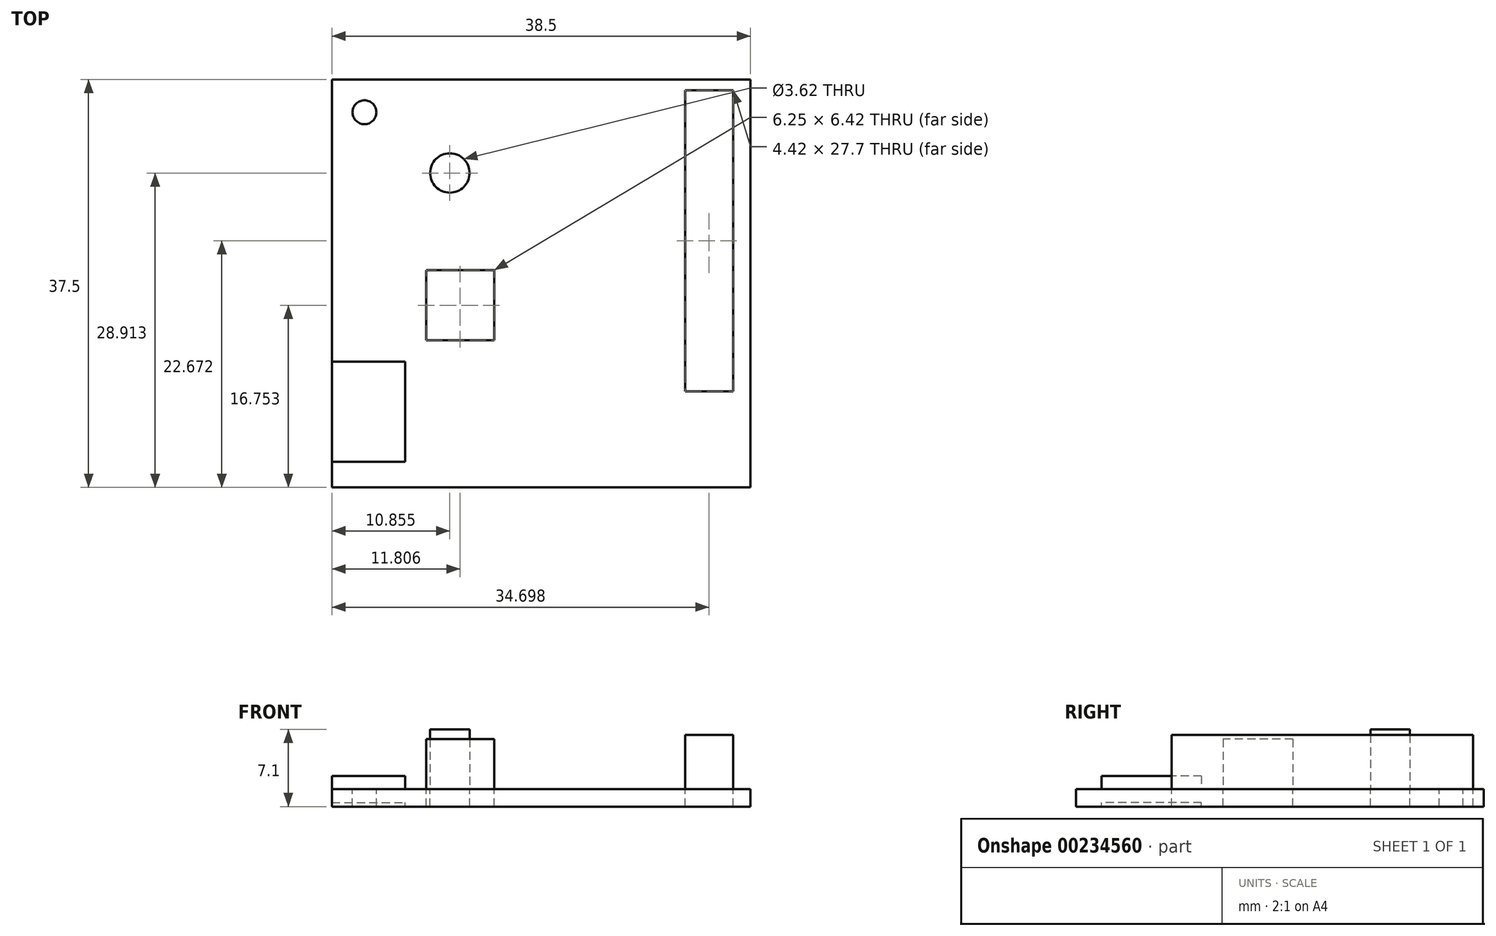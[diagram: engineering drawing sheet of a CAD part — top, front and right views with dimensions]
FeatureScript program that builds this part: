
annotation { "Feature Type Name" : "Feature", "Feature Type Description" : "" }
export const myFeature = defineFeature(function(context is Context, id is Id, definition is map)
    precondition{}
    {
        {
            var Q0;
            Q0=qCreatedBy(makeId("Top.planeOp"),FACE);
            var sketch = newSketch(context, id + "F0", { "sketchPlane" : qUnion([Q0])});
            skLineSegment(sketch, "E0.bottom", {"start": v(19.25, 18.75) * mm, "end": v(-19.25, 18.75) * mm});
            skLineSegment(sketch, "E0.top", {"start": v(19.25, -18.75) * mm, "end": v(-19.25, -18.75) * mm});
            skLineSegment(sketch, "E0.left", {"start": v(19.25, 18.75) * mm, "end": v(19.25, -18.75) * mm});
            skLineSegment(sketch, "E0.right", {"start": v(-19.25, 18.75) * mm, "end": v(-19.25, -18.75) * mm});
            skPoint(sketch, "E0.middle", {"position": v(0, 0) * mm});
            skLineSegment(sketch, "E1.bottom", {"start": v(17.66, 17.77) * mm, "end": v(13.24, 17.77) * mm});
            skLineSegment(sketch, "E1.top", {"start": v(17.66, -9.93) * mm, "end": v(13.24, -9.93) * mm});
            skLineSegment(sketch, "E1.left", {"start": v(17.66, 17.77) * mm, "end": v(17.66, -9.93) * mm});
            skLineSegment(sketch, "E1.right", {"start": v(13.24, 17.77) * mm, "end": v(13.24, -9.93) * mm});
            skLineSegment(sketch, "E2.bottom", {"start": v(-4.32, 1.21) * mm, "end": v(-10.57, 1.21) * mm});
            skLineSegment(sketch, "E2.top", {"start": v(-4.32, -5.2) * mm, "end": v(-10.57, -5.2) * mm});
            skLineSegment(sketch, "E2.left", {"start": v(-4.32, 1.21) * mm, "end": v(-4.32, -5.2) * mm});
            skLineSegment(sketch, "E2.right", {"start": v(-10.57, 1.21) * mm, "end": v(-10.57, -5.2) * mm});
            skPoint(sketch, "E2.middle", {"position": v(-7.44, -2) * mm});
            skCircle(sketch, "E3", {"center": v(-8.4, 10.16) * mm, "radius": 1.81 * mm});
            skPoint(sketch, "E4", {"position": v(-16.25, 15.75) * mm});
            skLineSegment(sketch, "E5.bottom", {"start": v(-19.25, -7.2) * mm, "end": v(-12.5, -7.2) * mm});
            skLineSegment(sketch, "E5.top", {"start": v(-19.25, -16.4) * mm, "end": v(-12.5, -16.4) * mm});
            skLineSegment(sketch, "E5.left", {"start": v(-19.25, -7.2) * mm, "end": v(-19.25, -16.4) * mm});
            skLineSegment(sketch, "E5.right", {"start": v(-12.5, -7.2) * mm, "end": v(-12.5, -16.4) * mm});
            skSolve(sketch);
        }
        {
            var Q0;
            Q0=makeQuery(id+"F0.imprint","IMPRINT",FACE,{"disambiguationData":[TD([[makeQuery(id+"F0.imprint","IMPRINT",EDGE,{"derivedFrom":sQuery(id+"F0.wireOp",EDGE,"E0.bottom")}),1.0]])]});
            extrude(context, id + "F1", {"entities" : qUnion([Q0]), "oppositeDirection" : true, "depth" : 1.6 * mm});
        }
        {
            var Q0;
            Q0=makeQuery(id+"F0.imprint","IMPRINT",FACE,{"disambiguationData":[TD([[makeQuery(id+"F0.imprint","IMPRINT",EDGE,{"derivedFrom":sQuery(id+"F0.wireOp",EDGE,"E1.bottom")}),1.0]])]});
            extrude(context, id + "F2", {"entities" : qUnion([Q0]), "operationType" : NewBodyOperationType.ADD, "depth" : 5 * mm});
        }
        {
            var Q0;
            Q0=makeQuery(id+"F0.imprint","IMPRINT",FACE,{"disambiguationData":[TD([[makeQuery(id+"F0.imprint","IMPRINT",EDGE,{"derivedFrom":sQuery(id+"F0.wireOp",EDGE,"E2.bottom")}),1.0]])]});
            extrude(context, id + "F3", {"entities" : qUnion([Q0]), "operationType" : NewBodyOperationType.ADD, "depth" : 4.6 * mm});
        }
        {
            var Q0;
            Q0=makeQuery(id+"F0.imprint","IMPRINT",FACE,{"disambiguationData":[TD([[makeQuery(id+"F0.imprint","IMPRINT",EDGE,{"derivedFrom":sQuery(id+"F0.wireOp",EDGE,"E3")}),1.0]])]});
            extrude(context, id + "F4", {"entities" : qUnion([Q0]), "operationType" : NewBodyOperationType.ADD, "depth" : 5.5 * mm});
        }
        {
            var Q0;
            Q0=sQuery(id+"F0.wireOp",VERTEX,"E4");
            var Q1;
            Q1=makeQuery(id+"F1.opExtrude","SWEPT_BODY",BODY,{"disambiguationData":[OSD([sQuery(id+"F0.wireOp",EDGE,"E0.bottom"),sQuery(id+"F0.wireOp",EDGE,"E0.top"),sQuery(id+"F0.wireOp",EDGE,"E0.left"),sQuery(id+"F0.wireOp",EDGE,"E0.right"),sQuery(id+"F0.wireOp",EDGE,"E1.bottom"),sQuery(id+"F0.wireOp",EDGE,"E1.top"),sQuery(id+"F0.wireOp",EDGE,"E1.left"),sQuery(id+"F0.wireOp",EDGE,"E1.right"),sQuery(id+"F0.wireOp",EDGE,"E2.bottom"),sQuery(id+"F0.wireOp",EDGE,"E2.top"),sQuery(id+"F0.wireOp",EDGE,"E2.left"),sQuery(id+"F0.wireOp",EDGE,"E2.right"),sQuery(id+"F0.wireOp",EDGE,"E3")])]});
            hole(context, id + "F5", {"style" : HoleStyle.SIMPLE, "endStyle" : HoleEndStyle.THROUGH, "holeDiameter" : 2.2 * mm, "locations" : qUnion([Q0]), "scope" : qUnion([Q1]), "isTappedThrough" : true});
        }
        {
            var Q0;
            Q0=makeQuery(id+"F0.imprint","IMPRINT",FACE,{"disambiguationData":[TD([[makeQuery(id+"F0.imprint","IMPRINT",EDGE,{"derivedFrom":sQuery(id+"F0.wireOp",EDGE,"E5.bottom")}),-1.0]])]});
            extrude(context, id + "F6", {"entities" : qUnion([Q0]), "operationType" : NewBodyOperationType.ADD, "endBound" : BoundingType.SYMMETRIC, "depth" : 2.45 * mm});
        }
    });
